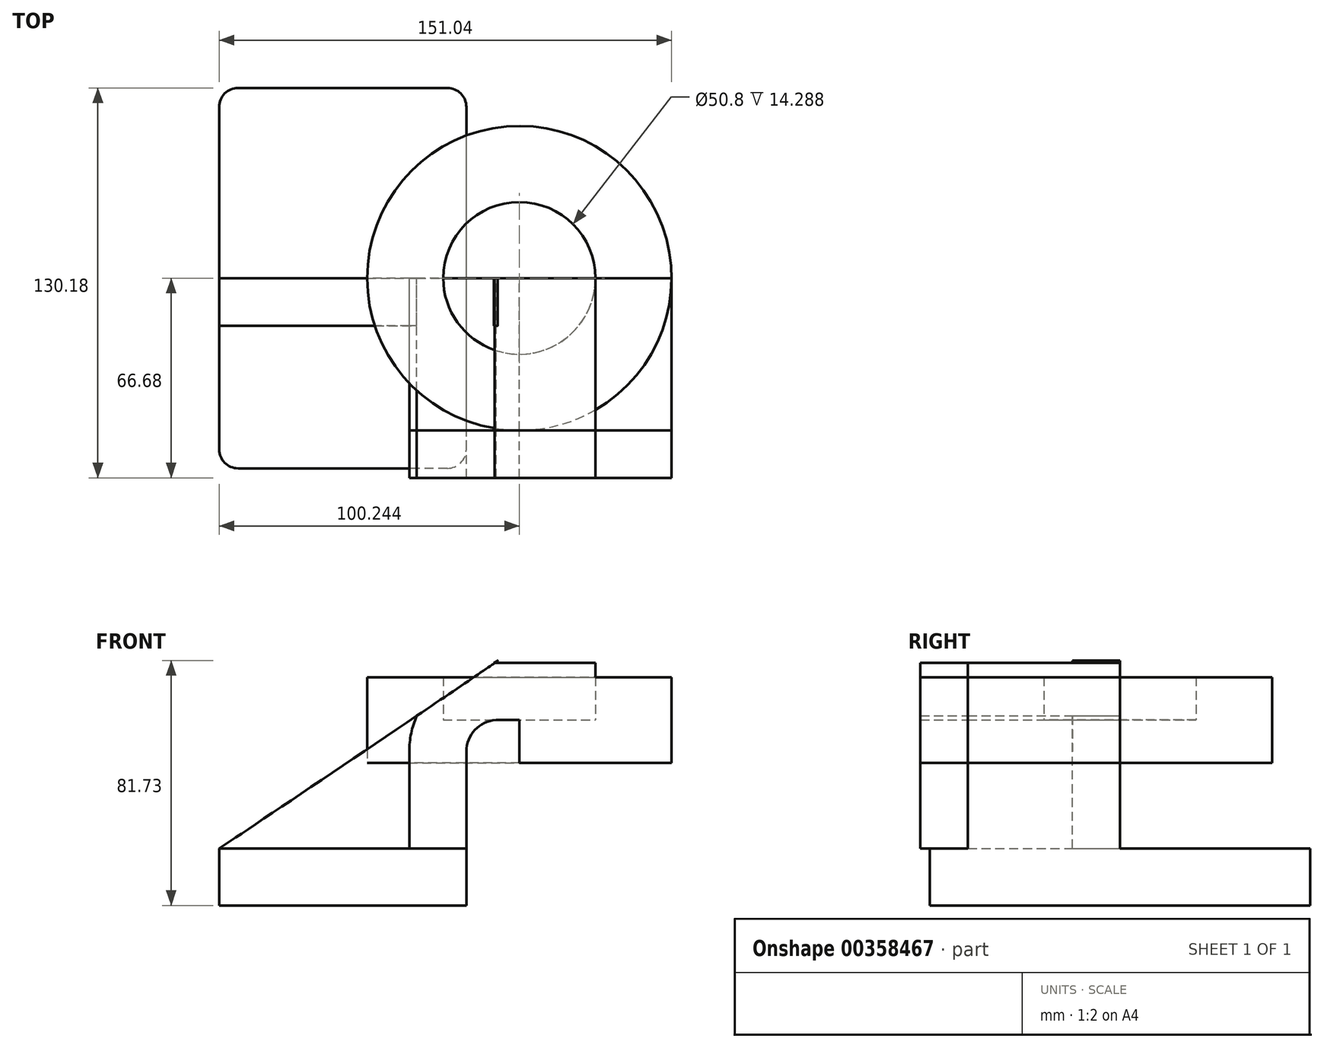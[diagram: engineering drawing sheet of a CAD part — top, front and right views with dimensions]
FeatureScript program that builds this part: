
annotation { "Feature Type Name" : "Feature", "Feature Type Description" : "" }
export const myFeature = defineFeature(function(context is Context, id is Id, definition is map)
    precondition{}
    {
        {
            var Q0;
            Q0=qCreatedBy(makeId("Front.planeOp"),FACE);
            var sketch = newSketch(context, id + "F0", { "sketchPlane" : qUnion([Q0])});
            skLineSegment(sketch, "E0.bottom", {"start": v(41.27, 9.53) * mm, "end": v(-41.28, 9.52) * mm});
            skLineSegment(sketch, "E0.top", {"start": v(41.28, -9.52) * mm, "end": v(-41.28, -9.53) * mm});
            skLineSegment(sketch, "E0.left", {"start": v(41.27, 9.53) * mm, "end": v(41.28, -9.52) * mm});
            skLineSegment(sketch, "E0.right", {"start": v(-41.28, 9.52) * mm, "end": v(-41.28, -9.53) * mm});
            skPoint(sketch, "E0.middle", {"position": v(0, 0) * mm});
            skLineSegment(sketch, "E1.bottom", {"start": v(58.96, 38.1) * mm, "end": v(109.76, 38.1) * mm});
            skLineSegment(sketch, "E1.top", {"start": v(58.96, 66.68) * mm, "end": v(109.76, 66.68) * mm});
            skLineSegment(sketch, "E1.left", {"start": v(58.96, 38.1) * mm, "end": v(58.96, 66.68) * mm});
            skLineSegment(sketch, "E1.right", {"start": v(109.76, 38.1) * mm, "end": v(109.76, 66.68) * mm});
            skPoint(sketch, "E1.middle", {"position": v(84.36, 52.39) * mm});
            skLineSegment(sketch, "E2", {"start": v(41.27, 9.53) * mm, "end": v(41.27, 41.86) * mm});
            skArc(sketch, "E3", {"start": v(41.28, 41.86) * mm, "mid": v(44.14, 49.08) * mm, "end": v(51.17, 52.39) * mm});
            skPoint(sketch, "E3.endSnap0", {"position": v(58.96, 52.39) * mm});
            skLineSegment(sketch, "E4", {"start": v(51.17, 52.39) * mm, "end": v(84.36, 52.39) * mm});
            skPoint(sketch, "E4.endSnap0", {"position": v(84.36, 38.1) * mm});
            skLineSegment(sketch, "E5.0", {"start": v(50.73, 71.44) * mm, "end": v(84.36, 71.44) * mm});
            skArc(sketch, "E5.1", {"start": v(22.22, 41.86) * mm, "mid": v(30.51, 62.4) * mm, "end": v(50.73, 71.44) * mm});
            skLineSegment(sketch, "E6.0", {"start": v(22.22, 9.53) * mm, "end": v(22.22, 41.86) * mm});
            skLineSegment(sketch, "E7", {"start": v(84.36, 71.44) * mm, "end": v(84.36, 52.39) * mm});
            skFitSpline(sketch, "E8", {"points": [v(-41.28, 9.52) * mm, v(50.73, 71.44) * mm, v(10.2, 44.67) * mm, v(-41.28, 9.52) * mm]});
            skSolve(sketch);
        }
        {
            var Q0;
            Q0=makeQuery(id+"F0.imprint","IMPRINT",FACE,{"disambiguationData":[TD([[makeQuery(id+"F0.imprint","IMPRINT",EDGE,{"derivedFrom":sQuery(id+"F0.wireOp",EDGE,"E0.top")}),-1.0]])]});
            extrude(context, id + "F1", {"entities" : qUnion([Q0]), "endBound" : BoundingType.SYMMETRIC, "depth" : 127 * mm});
        }
        {
            var Q0;
            {var subQ13=sQuery(id+"F0.wireOp",EDGE,"E2");Q0=makeQuery(id+"F0.imprint","IMPRINT",FACE,{"disambiguationData":[TD([[makeQuery(id+"F0.imprint","IMPRINT",EDGE,{"derivedFrom":subQ13}),1.0]])]});}
            var Q1;
            {var subQ0=sQuery(id+"F0.wireOp",EDGE,"E1.left");var subQ1=sQuery(id+"F0.wireOp",EDGE,"E1.top");var subQ2=makeQuery(id+"F0.imprint","INTERSECT",VERTEX,{"derivedFrom":[subQ1,subQ0]});Q1=makeQuery(id+"F0.imprint","IMPRINT",FACE,{"disambiguationData":[TD([[makeQuery(id+"F0.imprint","IMPRINT",EDGE,{"disambiguationData":[TD([[subQ2,-1.0]])],"derivedFrom":subQ1}),-1.0]])]});}
            var Q2;
            {var subQ1=sQuery(id+"F0.wireOp",EDGE,"E1.bottom");Q2=makeQuery(id+"F0.imprint","IMPRINT",FACE,{"disambiguationData":[TD([[makeQuery(id+"F0.imprint","IMPRINT",EDGE,{"derivedFrom":subQ1}),1.0]])]});}
            var Q3;
            {var subQ0=sQuery(id+"F0.wireOp",EDGE,"E8");var subQ1=sQuery(id+"F0.wireOp",EDGE,"E5.1");var subQ2=makeQuery(id+"F0.imprint","INTERSECT",VERTEX,{"disambiguationData":[OD(0.0)],"derivedFrom":[subQ1,subQ0]});Q3=makeQuery(id+"F0.imprint","IMPRINT",FACE,{"disambiguationData":[TD([[makeQuery(id+"F0.imprint","IMPRINT",EDGE,{"disambiguationData":[TD([[subQ2,-1.0]])],"derivedFrom":subQ1}),-1.0]])]});}
            extrude(context, id + "F2", {"entities" : qUnion([Q0, Q1, Q2, Q3]), "operationType" : NewBodyOperationType.ADD, "depth" : 50.8 * mm});
        }
        {
            var Q0;
            {var subQ3=sQuery(id+"F0.wireOp",EDGE,"E6.0");Q0=makeQuery(id+"F0.imprint","IMPRINT",FACE,{"disambiguationData":[TD([[makeQuery(id+"F0.imprint","IMPRINT",EDGE,{"derivedFrom":subQ3}),1.0]])]});}
            var Q1;
            {var subQ0=sQuery(id+"F0.wireOp",EDGE,"E8");var subQ1=sQuery(id+"F0.wireOp",EDGE,"E5.1");var subQ2=makeQuery(id+"F0.imprint","INTERSECT",VERTEX,{"disambiguationData":[OD(0.0)],"derivedFrom":[subQ1,subQ0]});Q1=makeQuery(id+"F0.imprint","IMPRINT",FACE,{"disambiguationData":[TD([[makeQuery(id+"F0.imprint","IMPRINT",EDGE,{"disambiguationData":[TD([[subQ2,1.0]])],"derivedFrom":subQ1}),-1.0]])]});}
            var Q2;
            Q2=makeQuery(id+"F2.opExtrude","CAP_FACE",FACE,{"disambiguationData":[OSD([sQuery(id+"F0.wireOp",EDGE,"E5.1"),sQuery(id+"F0.wireOp",EDGE,"E8")])],"isStart":false});
            extrude(context, id + "F3", {"entities" : qUnion([Q0, Q1, Q2]), "depth" : 15.88 * mm});
        }
        {
            var Q0;
            {var subQ1=sQuery(id+"F0.wireOp",EDGE,"E1.bottom");Q0=makeQuery(id+"F0.imprint","IMPRINT",FACE,{"disambiguationData":[TD([[makeQuery(id+"F0.imprint","IMPRINT",EDGE,{"derivedFrom":subQ1}),1.0]])]});}
            var Q1;
            Q1=sQuery(id+"F0.wireOp",EDGE,"E1.left");
            revolve(context, id + "F4", {"entities" : qUnion([Q0]), "axis" : qUnion([Q1]), "revolveType" : RevolveType.FULL});
        }
        {
            var Q0;
            Q0=makeQuery(id+"F1.opExtrude","CAP_EDGE",EDGE,{"disambiguationData":[OSD([sQuery(id+"F0.wireOp",EDGE,"E0.left")])],"isStart":true});
            var Q1;
            Q1=makeQuery(id+"F1.opExtrude","CAP_EDGE",EDGE,{"disambiguationData":[OSD([sQuery(id+"F0.wireOp",EDGE,"E0.right")])],"isStart":true});
            var Q2;
            Q2=makeQuery(id+"F1.opExtrude","CAP_EDGE",EDGE,{"disambiguationData":[OSD([sQuery(id+"F0.wireOp",EDGE,"E0.right")])],"isStart":false});
            var Q3;
            Q3=makeQuery(id+"F1.opExtrude","CAP_EDGE",EDGE,{"disambiguationData":[OSD([sQuery(id+"F0.wireOp",EDGE,"E0.left")])],"isStart":false});
            fillet(context, id + "F5", {"entities" : qUnion([Q0, Q1, Q2, Q3]), "radius" : 6.35 * mm, "tangentPropagation" : true, "allowEdgeOverflow" : false});
        }
    });
